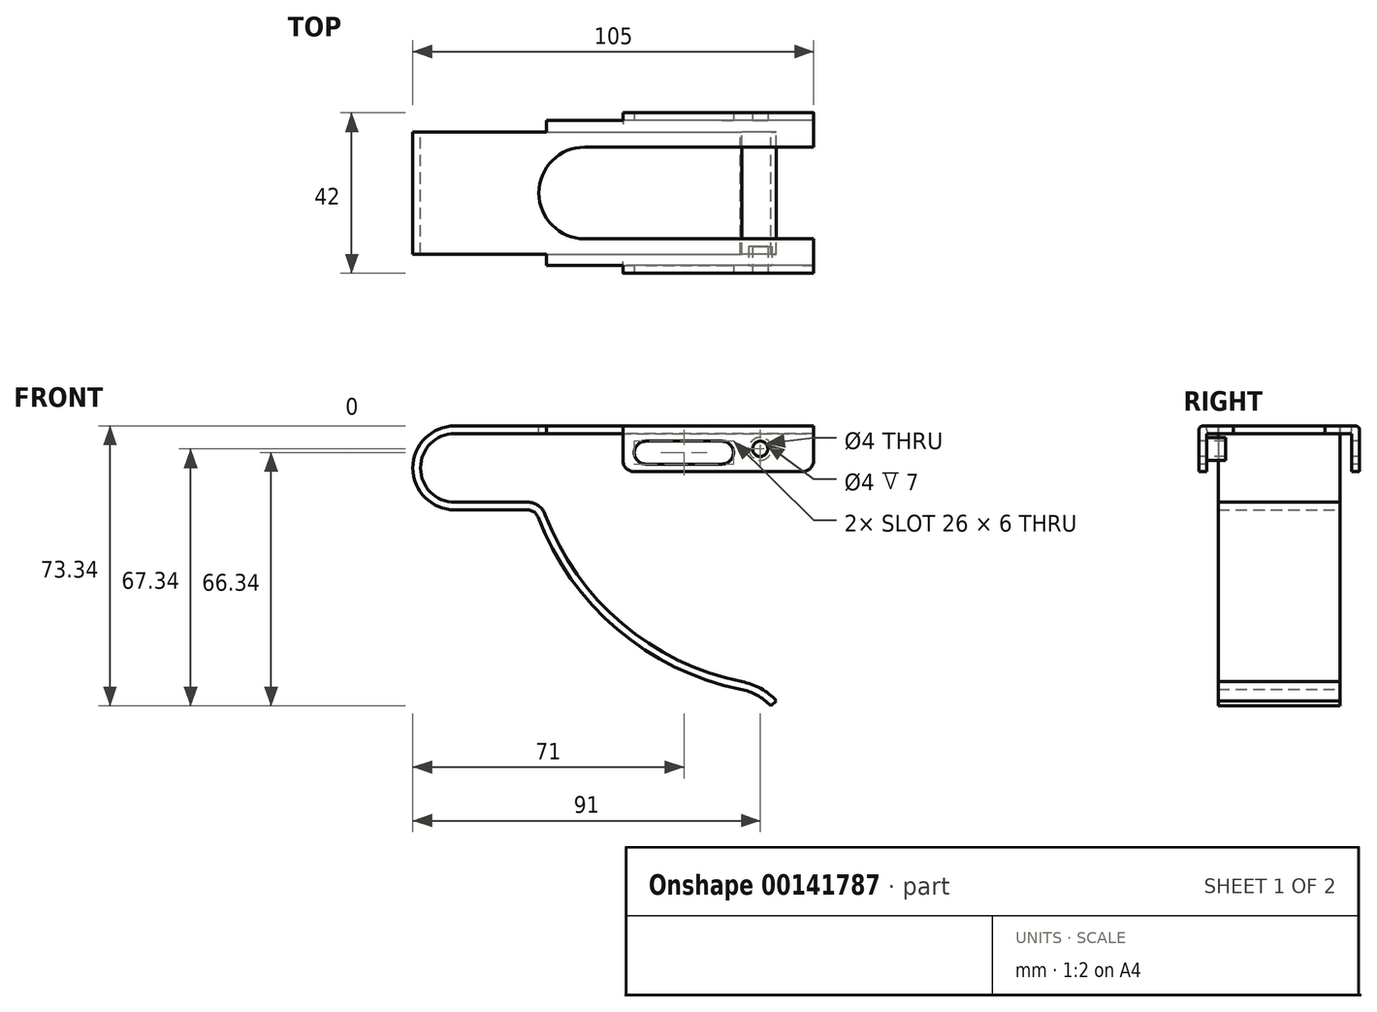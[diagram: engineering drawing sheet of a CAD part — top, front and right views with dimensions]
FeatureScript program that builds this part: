
annotation { "Feature Type Name" : "Feature", "Feature Type Description" : "" }
export const myFeature = defineFeature(function(context is Context, id is Id, definition is map)
    precondition{}
    {
        {
            var Q0;
            Q0=qCreatedBy(makeId("Front.planeOp"),FACE);
            var sketch = newSketch(context, id + "F0", { "sketchPlane" : qUnion([Q0])});
            skArc(sketch, "E0", {"start": v(0, 9) * mm, "mid": v(-9, 0) * mm, "end": v(0, -9) * mm});
            skLineSegment(sketch, "E1", {"start": v(0, 9) * mm, "end": v(94, 9) * mm});
            skLineSegment(sketch, "E2", {"start": v(0, -9) * mm, "end": v(19, -9) * mm});
            skArc(sketch, "E3", {"start": v(23.67, -12.23) * mm, "mid": v(43.8, -40.75) * mm, "end": v(75.2, -56) * mm});
            skArc(sketch, "E4", {"start": v(84.25, -61) * mm, "mid": v(80.14, -57.75) * mm, "end": v(75.2, -56) * mm});
            skPoint(sketch, "E5.visualSharp", {"position": v(22.54, -9) * mm});
            skArc(sketch, "E5.filletArc", {"start": v(23.67, -12.23) * mm, "mid": v(21.84, -9.88) * mm, "end": v(19, -9) * mm});
            skLineSegment(sketch, "E6.0", {"start": v(0, 11) * mm, "end": v(94, 11) * mm});
            skArc(sketch, "E6.1", {"start": v(0, 11) * mm, "mid": v(-11, 0) * mm, "end": v(0, -11) * mm});
            skArc(sketch, "E6.2", {"start": v(82.77, -62.34) * mm, "mid": v(79.16, -59.5) * mm, "end": v(74.83, -57.97) * mm});
            skArc(sketch, "E6.3", {"start": v(21.8, -12.94) * mm, "mid": v(42.52, -42.28) * mm, "end": v(74.83, -57.97) * mm});
            skArc(sketch, "E6.4", {"start": v(21.8, -12.94) * mm, "mid": v(20.7, -11.53) * mm, "end": v(19, -11) * mm});
            skLineSegment(sketch, "E6.5", {"start": v(0, -11) * mm, "end": v(19, -11) * mm});
            skLineSegment(sketch, "E7", {"start": v(94, 9) * mm, "end": v(94, 11) * mm});
            skLineSegment(sketch, "E8", {"start": v(82.77, -62.34) * mm, "end": v(84.25, -61) * mm});
            skSolve(sketch);
        }
        {
            var Q0;
            Q0 = qSketchRegion(id + "F0", true);
            extrude(context, id + "F1", {"entities" : qUnion([Q0]), "depth" : 16 * mm});
        }
        {
            var Q0;
            Q0=makeQuery(id+"F1.opExtrude","SWEPT_FACE",FACE,{"disambiguationData":[OSD([sQuery(id+"F0.wireOp",EDGE,"E6.0")])]});
            var sketch = newSketch(context, id + "F2", { "sketchPlane" : qUnion([Q0])});
            skLineSegment(sketch, "E9.bottom", {"start": v(94, -16) * mm, "end": v(24, -16) * mm});
            skLineSegment(sketch, "E9.top", {"start": v(94, -19) * mm, "end": v(24, -19) * mm});
            skLineSegment(sketch, "E9.left", {"start": v(94, -16) * mm, "end": v(94, -19) * mm});
            skLineSegment(sketch, "E9.right", {"start": v(24, -16) * mm, "end": v(24, -19) * mm});
            skSolve(sketch);
        }
        {
            var Q0;
            Q0 = qSketchRegion(id + "F2", true);
            extrude(context, id + "F3", {"entities" : qUnion([Q0]), "operationType" : NewBodyOperationType.ADD, "oppositeDirection" : true, "depth" : 2 * mm});
        }
        {
            var Q0;
            Q0=makeQuery(id+"F3.opExtrude","SWEPT_FACE",FACE,{"disambiguationData":[OSD([sQuery(id+"F2.wireOp",EDGE,"E9.top")])]});
            var sketch = newSketch(context, id + "F4", { "sketchPlane" : qUnion([Q0])});
            skLineSegment(sketch, "E10.bottom", {"start": v(94, 11) * mm, "end": v(44, 11) * mm});
            skLineSegment(sketch, "E10.top", {"start": v(94, -1) * mm, "end": v(44, -1) * mm});
            skLineSegment(sketch, "E10.left", {"start": v(94, 11) * mm, "end": v(94, -1) * mm});
            skLineSegment(sketch, "E10.right", {"start": v(44, 11) * mm, "end": v(44, -1) * mm});
            skSolve(sketch);
        }
        {
            var Q0;
            Q0 = qSketchRegion(id + "F4", true);
            extrude(context, id + "F5", {"entities" : qUnion([Q0]), "operationType" : NewBodyOperationType.ADD, "depth" : 2 * mm});
        }
        {
            var Q0;
            Q0=makeQuery(id+"F5.opExtrude","CAP_EDGE",EDGE,{"disambiguationData":[OSD([sQuery(id+"F4.wireOp",EDGE,"E10.bottom")])],"isStart":false});
            var Q1;
            {var subQ0=sQuery(id+"F2.wireOp",EDGE,"E9.top");Q1=makeQuery(id+"F5.boolean.opBoolean","SPLIT",EDGE,{"disambiguationData":[TD([makeQuery(id+"F1.opExtrude","SWEPT_FACE",FACE,{"disambiguationData":[OSD([sQuery(id+"F0.wireOp",EDGE,"E7")])]})])],"derivedFrom":makeQuery(id+"F3.opExtrude","CAP_EDGE",EDGE,{"disambiguationData":[OSD([subQ0])],"isStart":false})});}
            fillet(context, id + "F6", {"entities" : qUnion([Q0, Q1]), "radius" : 1 * mm, "allowEdgeOverflow" : false});
        }
        {
            var Q0;
            Q0=makeQuery(id+"F1.opExtrude","SWEPT_BODY",BODY,{"disambiguationData":[OSD([sQuery(id+"F0.wireOp",EDGE,"E0"),sQuery(id+"F0.wireOp",EDGE,"E1"),sQuery(id+"F0.wireOp",EDGE,"E2"),sQuery(id+"F0.wireOp",EDGE,"E3"),sQuery(id+"F0.wireOp",EDGE,"E4"),sQuery(id+"F0.wireOp",EDGE,"E5.filletArc"),sQuery(id+"F0.wireOp",EDGE,"E6.0"),sQuery(id+"F0.wireOp",EDGE,"E6.1"),sQuery(id+"F0.wireOp",EDGE,"E6.2"),sQuery(id+"F0.wireOp",EDGE,"E6.3"),sQuery(id+"F0.wireOp",EDGE,"E6.4"),sQuery(id+"F0.wireOp",EDGE,"E6.5"),sQuery(id+"F0.wireOp",EDGE,"E7"),sQuery(id+"F0.wireOp",EDGE,"E8")])]});
            var Q1;
            Q1=qCreatedBy(makeId("Front.planeOp"),FACE);
            mirror(context, id + "F7", {"operationType" : NewBodyOperationType.ADD, "entities" : qUnion([Q0]), "mirrorPlane" : qUnion([Q1])});
        }
        {
            var Q0;
            {var subQ0=makeQuery(id+"F5.boolean.opBoolean","MERGE",FACE,{"derivedFrom":[makeQuery(id+"F3.boolean.opBoolean","MERGE",FACE,{"derivedFrom":[makeQuery(id+"F1.opExtrude","SWEPT_FACE",FACE,{"disambiguationData":[OSD([sQuery(id+"F0.wireOp",EDGE,"E6.0")])]}),makeQuery(id+"F3.opExtrude","CAP_FACE",FACE,{"disambiguationData":[OSD([sQuery(id+"F2.wireOp",EDGE,"E9.bottom"),sQuery(id+"F2.wireOp",EDGE,"E9.top"),sQuery(id+"F2.wireOp",EDGE,"E9.left"),sQuery(id+"F2.wireOp",EDGE,"E9.right")])],"isStart":true})]}),makeQuery(id+"F5.opExtrude","SWEPT_FACE",FACE,{"disambiguationData":[OSD([sQuery(id+"F4.wireOp",EDGE,"E10.bottom")])]})]});Q0=makeQuery(id+"F7.boolean.opBoolean","MERGE",FACE,{"derivedFrom":[subQ0,makeQuery(id+"F7.opPattern","COPY",FACE,{"derivedFrom":subQ0,"instanceName":"1"})]});}
            var sketch = newSketch(context, id + "F8", { "sketchPlane" : qUnion([Q0])});
            skArc(sketch, "E11", {"start": v(34, 12) * mm, "mid": v(22, 0) * mm, "end": v(34, -12) * mm});
            skLineSegment(sketch, "E12", {"start": v(34, 12) * mm, "end": v(94, 12) * mm});
            skLineSegment(sketch, "E13", {"start": v(34, -12) * mm, "end": v(94, -12) * mm});
            skLineSegment(sketch, "E14", {"start": v(94, 12) * mm, "end": v(94, -12) * mm});
            skSolve(sketch);
        }
        {
            var Q0;
            Q0 = qSketchRegion(id + "F8", true);
            extrude(context, id + "F9", {"entities" : qUnion([Q0]), "operationType" : NewBodyOperationType.REMOVE, "oppositeDirection" : true, "depth" : 2 * mm});
        }
        {
            var Q0;
            Q0=makeQuery(id+"F5.opExtrude","CAP_FACE",FACE,{"disambiguationData":[OSD([sQuery(id+"F4.wireOp",EDGE,"E10.bottom"),sQuery(id+"F4.wireOp",EDGE,"E10.top"),sQuery(id+"F4.wireOp",EDGE,"E10.left"),sQuery(id+"F4.wireOp",EDGE,"E10.right")])],"isStart":false});
            var sketch = newSketch(context, id + "F10", { "sketchPlane" : qUnion([Q0])});
            skLineSegment(sketch, "E15", {"start": v(50, 4) * mm, "end": v(70, 4) * mm});
            skArc(sketch, "E16.0.startCap", {"start": v(50, 1) * mm, "mid": v(47, 4) * mm, "end": v(50, 7) * mm});
            skArc(sketch, "E16.0.endCap", {"start": v(70, 7) * mm, "mid": v(73, 4) * mm, "end": v(70, 1) * mm});
            skLineSegment(sketch, "E16.0.left", {"start": v(50, 7) * mm, "end": v(70, 7) * mm});
            skLineSegment(sketch, "E16.0.right", {"start": v(50, 1) * mm, "end": v(70, 1) * mm});
            skSolve(sketch);
        }
        {
            var Q0;
            Q0 = qSketchRegion(id + "F10", true);
            extrude(context, id + "F11", {"entities" : qUnion([Q0]), "operationType" : NewBodyOperationType.REMOVE, "endBound" : BoundingType.THROUGH_ALL, "oppositeDirection" : true, "depth" : 25 * mm});
        }
        {
            var Q0;
            Q0=makeQuery(id+"F5.opExtrude","CAP_FACE",FACE,{"disambiguationData":[OSD([sQuery(id+"F4.wireOp",EDGE,"E10.bottom"),sQuery(id+"F4.wireOp",EDGE,"E10.top"),sQuery(id+"F4.wireOp",EDGE,"E10.left"),sQuery(id+"F4.wireOp",EDGE,"E10.right")])],"isStart":false});
            var sketch = newSketch(context, id + "F12", { "sketchPlane" : qUnion([Q0])});
            skPoint(sketch, "E17", {"position": v(80, 5) * mm});
            skSolve(sketch);
        }
        {
            var Q0;
            Q0=sQuery(id+"F12.wireOp",VERTEX,"E17");
            var Q1;
            Q1=makeQuery(id+"F1.opExtrude","SWEPT_BODY",BODY,{"disambiguationData":[OSD([sQuery(id+"F0.wireOp",EDGE,"E0"),sQuery(id+"F0.wireOp",EDGE,"E1"),sQuery(id+"F0.wireOp",EDGE,"E2"),sQuery(id+"F0.wireOp",EDGE,"E3"),sQuery(id+"F0.wireOp",EDGE,"E4"),sQuery(id+"F0.wireOp",EDGE,"E5.filletArc"),sQuery(id+"F0.wireOp",EDGE,"E6.0"),sQuery(id+"F0.wireOp",EDGE,"E6.1"),sQuery(id+"F0.wireOp",EDGE,"E6.2"),sQuery(id+"F0.wireOp",EDGE,"E6.3"),sQuery(id+"F0.wireOp",EDGE,"E6.4"),sQuery(id+"F0.wireOp",EDGE,"E6.5"),sQuery(id+"F0.wireOp",EDGE,"E7"),sQuery(id+"F0.wireOp",EDGE,"E8")])]});
            hole(context, id + "F13", {"style" : HoleStyle.SIMPLE, "endStyle" : HoleEndStyle.THROUGH, "holeDiameter" : 4 * mm, "locations" : qUnion([Q0]), "scope" : qUnion([Q1]), "isTappedThrough" : true});
        }
        {
            var Q0;
            Q0=makeQuery(id+"F5.opExtrude","CAP_FACE",FACE,{"disambiguationData":[OSD([sQuery(id+"F4.wireOp",EDGE,"E10.bottom"),sQuery(id+"F4.wireOp",EDGE,"E10.top"),sQuery(id+"F4.wireOp",EDGE,"E10.left"),sQuery(id+"F4.wireOp",EDGE,"E10.right")])],"isStart":true});
            var sketch = newSketch(context, id + "F14", { "sketchPlane" : qUnion([Q0])});
            skCircle(sketch, "E18.0", {"center": v(-80, 5) * mm, "radius": 2 * mm});
            skCircle(sketch, "E19.0", {"center": v(-80, 5) * mm, "radius": 3 * mm});
            skSolve(sketch);
        }
        {
            var Q0;
            Q0 = qSketchRegion(id + "F14", true);
            extrude(context, id + "F15", {"entities" : qUnion([Q0]), "operationType" : NewBodyOperationType.ADD, "depth" : 5 * mm});
        }
        {
            var Q0;
            Q0=makeQuery(id+"F5.opExtrude","SWEPT_EDGE",EDGE,{"disambiguationData":[OSD([sQuery(id+"F4.wireOp",EDGE,"E10.top"),sQuery(id+"F4.wireOp",EDGE,"E10.left")])]});
            var Q1;
            Q1=makeQuery(id+"F7.opPattern","COPY",EDGE,{"derivedFrom":makeQuery(id+"F5.opExtrude","SWEPT_EDGE",EDGE,{"disambiguationData":[OSD([sQuery(id+"F4.wireOp",EDGE,"E10.top"),sQuery(id+"F4.wireOp",EDGE,"E10.left")])]}),"instanceName":"1"});
            var Q2;
            Q2=makeQuery(id+"F7.opPattern","COPY",EDGE,{"derivedFrom":makeQuery(id+"F5.opExtrude","SWEPT_EDGE",EDGE,{"disambiguationData":[OSD([sQuery(id+"F4.wireOp",EDGE,"E10.top"),sQuery(id+"F4.wireOp",EDGE,"E10.right")])]}),"instanceName":"1"});
            var Q3;
            Q3=makeQuery(id+"F5.opExtrude","SWEPT_EDGE",EDGE,{"disambiguationData":[OSD([sQuery(id+"F4.wireOp",EDGE,"E10.top"),sQuery(id+"F4.wireOp",EDGE,"E10.right")])]});
            fillet(context, id + "F16", {"entities" : qUnion([Q0, Q1, Q2, Q3]), "radius" : 3 * mm, "tangentPropagation" : true, "allowEdgeOverflow" : false});
        }
    });
